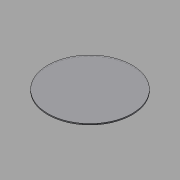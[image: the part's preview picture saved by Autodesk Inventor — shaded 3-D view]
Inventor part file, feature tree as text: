
AUTODESK INVENTOR PART (.ipt)
format: ipt  version: 2015 (Build 190159000, 159)  size: 82,944 bytes
history: native  units: mm
features: extrude x1, sketch x1
ambient origin geometry x8: Origin, YZ Plane, XZ Plane, XY Plane, X Axis, Y Axis, Z Axis, Center Point
bodies: Solid1 (feature_tree)
feature tree (2):
  extrude  "Extrusion1"  Depth=1.0mm TaperAngle=0.0deg
  sketch  "Sketch1"  dims[d0=65.0mm d1=1.0mm d2=0.0mm]
